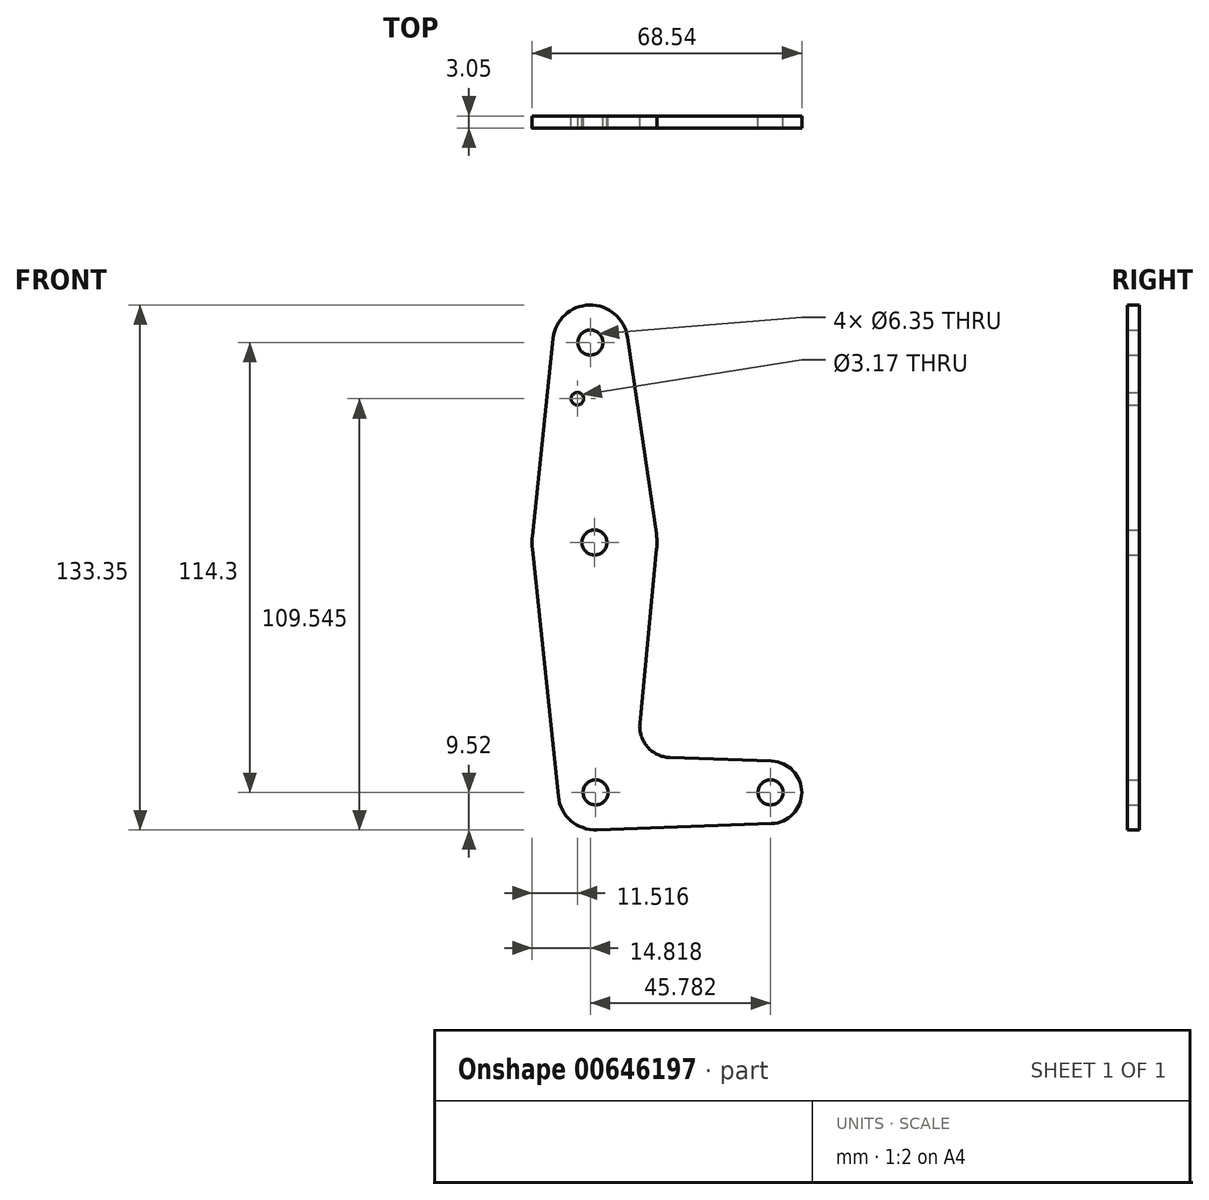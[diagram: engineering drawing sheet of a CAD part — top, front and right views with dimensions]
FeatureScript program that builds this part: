
annotation { "Feature Type Name" : "Feature", "Feature Type Description" : "" }
export const myFeature = defineFeature(function(context is Context, id is Id, definition is map)
    precondition{}
    {
        {
            var Q0;
            Q0=qCreatedBy(makeId("Front.planeOp"),FACE);
            var sketch = newSketch(context, id + "F0", { "sketchPlane" : qUnion([Q0])});
            skLineSegment(sketch, "E0", {"start": v(0, 0) * mm, "end": v(44.45, 0) * mm});
            skCircle(sketch, "E1", {"center": v(-1.33, 114.3) * mm, "radius": 9.53 * mm});
            skCircle(sketch, "E2", {"center": v(44.45, 0) * mm, "radius": 7.94 * mm});
            skPoint(sketch, "E3", {"position": v(-0.28, 63.5) * mm});
            skCircle(sketch, "E4", {"center": v(-0.28, 63.5) * mm, "radius": 15.88 * mm});
            skLineSegment(sketch, "E5", {"start": v(-10.8, 115.3) * mm, "end": v(-16.07, 65.16) * mm});
            skLineSegment(sketch, "E6", {"start": v(8.1, 115.69) * mm, "end": v(15.53, 65.16) * mm});
            skLineSegment(sketch, "E7", {"start": v(15.53, 61.98) * mm, "end": v(11.26, 17.56) * mm});
            skLineSegment(sketch, "E8", {"start": v(-16.07, 61.84) * mm, "end": v(-9.47, -1) * mm});
            skLineSegment(sketch, "E9", {"start": v(18.89, 8.85) * mm, "end": v(44.73, 7.93) * mm});
            skLineSegment(sketch, "E10", {"start": v(0, -9.53) * mm, "end": v(44.73, -7.93) * mm});
            skCircle(sketch, "E11", {"center": v(-1.33, 114.3) * mm, "radius": 3.18 * mm});
            skCircle(sketch, "E12", {"center": v(-0.28, 63.5) * mm, "radius": 3.18 * mm});
            skCircle(sketch, "E13", {"center": v(0, 0) * mm, "radius": 3.18 * mm});
            skCircle(sketch, "E14", {"center": v(44.45, 0) * mm, "radius": 3.18 * mm});
            skLineSegment(sketch, "E15", {"start": v(-0.28, 63.5) * mm, "end": v(-1.33, 114.29) * mm});
            skLineSegment(sketch, "E16", {"start": v(-0.28, 63.5) * mm, "end": v(0, 0) * mm});
            skCircle(sketch, "E17", {"center": v(-4.63, 100.02) * mm, "radius": 1.59 * mm});
            skPoint(sketch, "E18.newPointA", {"position": v(9.47, -1) * mm});
            skPoint(sketch, "E18.newPointB", {"position": v(0, 9.53) * mm});
            skArc(sketch, "E18.filletArc", {"start": v(11.26, 17.56) * mm, "mid": v(13.2, 11.56) * mm, "end": v(18.89, 8.85) * mm});
            skCircle(sketch, "E19", {"center": v(0, 0) * mm, "radius": 9.53 * mm});
            skSolve(sketch);
        }
        {
            var Q0;
            {var subQ4=sQuery(id+"F0.wireOp",EDGE,"E13");var subQ6=sQuery(id+"F0.wireOp",EDGE,"E0");var subQ7=makeQuery(id+"F0.imprint","INTERSECT",VERTEX,{"derivedFrom":[subQ6,subQ4]});Q0=makeQuery(id+"F0.imprint","IMPRINT",FACE,{"disambiguationData":[TD([[makeQuery(id+"F0.imprint","IMPRINT",EDGE,{"disambiguationData":[TD([[subQ7,-1.0]])],"derivedFrom":subQ6}),-1.0]])]});}
            var Q1;
            {var subQ0=sQuery(id+"F0.wireOp",EDGE,"E13");var subQ1=sQuery(id+"F0.wireOp",EDGE,"E0");var subQ2=makeQuery(id+"F0.imprint","INTERSECT",VERTEX,{"derivedFrom":[subQ1,subQ0]});Q1=makeQuery(id+"F0.imprint","IMPRINT",FACE,{"disambiguationData":[TD([[makeQuery(id+"F0.imprint","IMPRINT",EDGE,{"disambiguationData":[TD([[subQ2,-1.0]])],"derivedFrom":subQ1}),1.0]])]});}
            var Q2;
            {var subQ0=sQuery(id+"F0.wireOp",EDGE,"E2");var subQ1=sQuery(id+"F0.wireOp",EDGE,"E0");var subQ2=makeQuery(id+"F0.imprint","INTERSECT",VERTEX,{"derivedFrom":[subQ1,subQ0]});Q2=makeQuery(id+"F0.imprint","IMPRINT",FACE,{"disambiguationData":[TD([[makeQuery(id+"F0.imprint","IMPRINT",EDGE,{"disambiguationData":[TD([[subQ2,1.0]])],"derivedFrom":subQ1}),-1.0]])]});}
            var Q3;
            {var subQ0=sQuery(id+"F0.wireOp",EDGE,"E7");Q3=makeQuery(id+"F0.imprint","IMPRINT",FACE,{"disambiguationData":[TD([[makeQuery(id+"F0.imprint","IMPRINT",EDGE,{"derivedFrom":subQ0}),-1.0]])]});}
            var Q4;
            {var subQ0=sQuery(id+"F0.wireOp",EDGE,"E8");Q4=makeQuery(id+"F0.imprint","IMPRINT",FACE,{"disambiguationData":[TD([[makeQuery(id+"F0.imprint","IMPRINT",EDGE,{"derivedFrom":subQ0}),1.0]])]});}
            var Q5;
            Q5=makeQuery(id+"F0.imprint","IMPRINT",FACE,{"disambiguationData":[TD([[makeQuery(id+"F0.imprint","IMPRINT",EDGE,{"derivedFrom":sQuery(id+"F0.wireOp",EDGE,"E14")}),-1.0]])]});
            var Q6;
            {var subQ5=sQuery(id+"F0.wireOp",EDGE,"E4");var subQ6=makeQuery(id+"F0.imprint","INTERSECT",VERTEX,{"derivedFrom":[subQ5,sQuery(id+"F0.wireOp",EDGE,"E5")]});Q6=makeQuery(id+"F0.imprint","IMPRINT",FACE,{"disambiguationData":[TD([[makeQuery(id+"F0.imprint","IMPRINT",EDGE,{"disambiguationData":[TD([[subQ6,1.0]])],"derivedFrom":subQ5}),1.0]])]});}
            var Q7;
            {var subQ5=sQuery(id+"F0.wireOp",EDGE,"E4");var subQ8=makeQuery(id+"F0.imprint","INTERSECT",VERTEX,{"derivedFrom":[subQ5,sQuery(id+"F0.wireOp",EDGE,"E6")]});Q7=makeQuery(id+"F0.imprint","IMPRINT",FACE,{"disambiguationData":[TD([[makeQuery(id+"F0.imprint","IMPRINT",EDGE,{"disambiguationData":[TD([[subQ8,-1.0]])],"derivedFrom":subQ5}),1.0]])]});}
            var Q8;
            {var subQ0=sQuery(id+"F0.wireOp",EDGE,"E6");var subQ1=sQuery(id+"F0.wireOp",EDGE,"E1");var subQ2=makeQuery(id+"F0.imprint","INTERSECT",VERTEX,{"derivedFrom":[subQ1,subQ0]});Q8=makeQuery(id+"F0.imprint","IMPRINT",FACE,{"disambiguationData":[TD([[makeQuery(id+"F0.imprint","IMPRINT",EDGE,{"disambiguationData":[TD([[subQ2,1.0]])],"derivedFrom":subQ1}),-1.0]])]});}
            var Q9;
            {var subQ0=sQuery(id+"F0.wireOp",EDGE,"E5");Q9=makeQuery(id+"F0.imprint","IMPRINT",FACE,{"disambiguationData":[TD([[makeQuery(id+"F0.imprint","IMPRINT",EDGE,{"derivedFrom":subQ0}),1.0]])]});}
            var Q10;
            Q10=makeQuery(id+"F0.imprint","IMPRINT",FACE,{"disambiguationData":[TD([[makeQuery(id+"F0.imprint","IMPRINT",EDGE,{"derivedFrom":sQuery(id+"F0.wireOp",EDGE,"E11")}),-1.0]])]});
            extrude(context, id + "F1", {"entities" : qUnion([Q0, Q1, Q2, Q3, Q4, Q5, Q6, Q7, Q8, Q9, Q10]), "depth" : 3.05 * mm, "offsetDistance" : 25.4 * mm});
        }
    });
